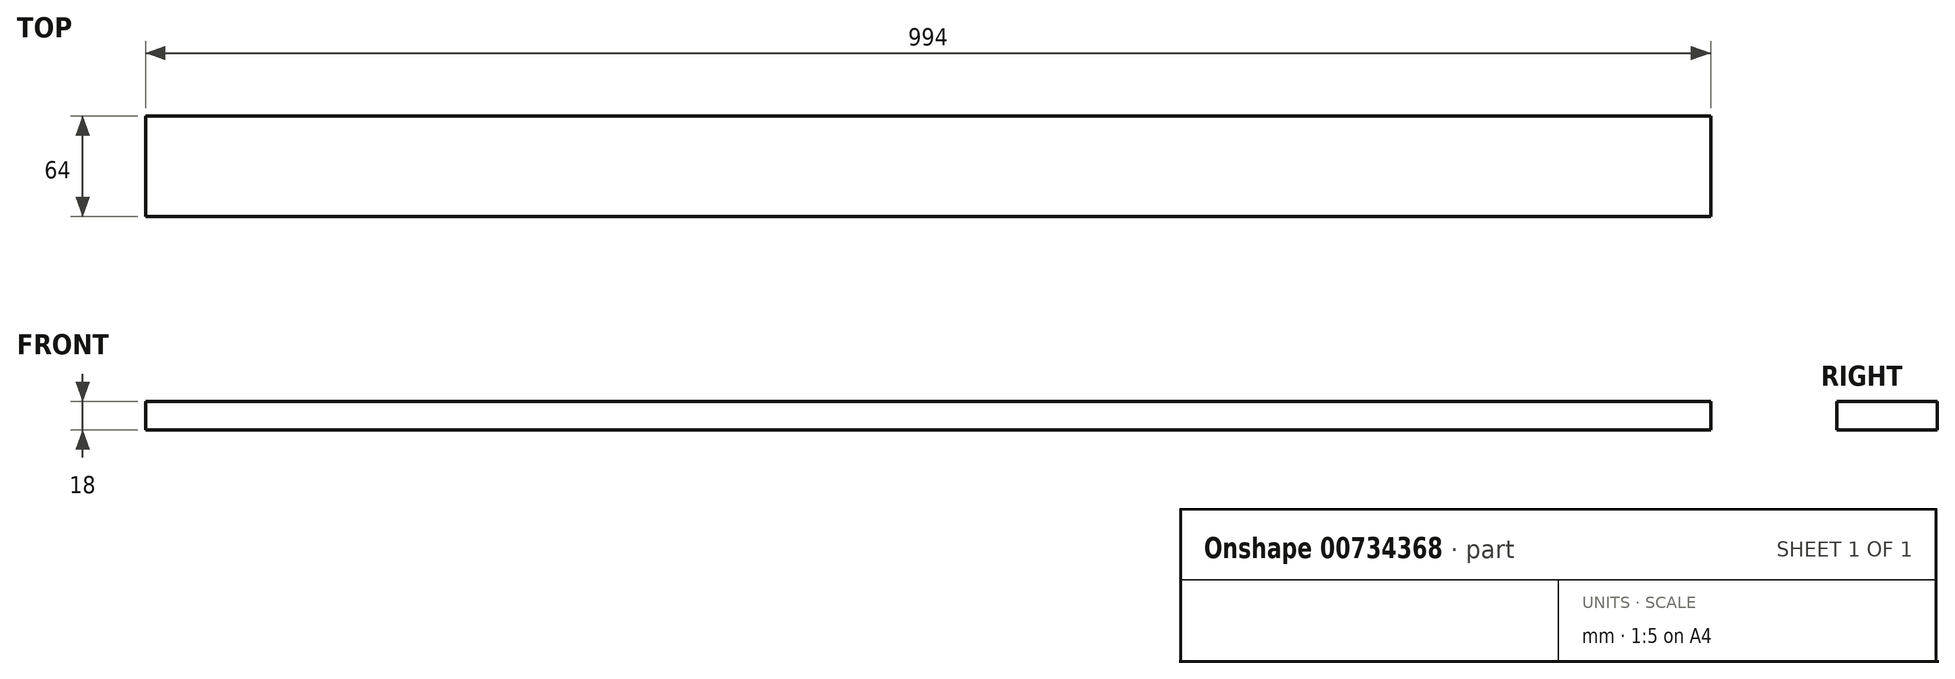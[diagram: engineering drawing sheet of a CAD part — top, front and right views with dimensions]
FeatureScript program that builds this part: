
annotation { "Feature Type Name" : "Feature", "Feature Type Description" : "" }
export const myFeature = defineFeature(function(context is Context, id is Id, definition is map)
    precondition{}
    {
        {
            var Q0;
            Q0=qCreatedBy(makeId("Top.planeOp"),FACE);
            var sketch = newSketch(context, id + "F0", { "sketchPlane" : qUnion([Q0])});
            skLineSegment(sketch, "E0.bottom", {"start": v(-497, -32) * mm, "end": v(497, -32) * mm});
            skLineSegment(sketch, "E0.top", {"start": v(-497, 32) * mm, "end": v(497, 32) * mm});
            skLineSegment(sketch, "E0.left", {"start": v(-497, -32) * mm, "end": v(-497, 32) * mm});
            skLineSegment(sketch, "E0.right", {"start": v(497, -32) * mm, "end": v(497, 32) * mm});
            skPoint(sketch, "E0.middle", {"position": v(0, 0) * mm});
            skSolve(sketch);
        }
        {
            var Q0;
            Q0 = qSketchRegion(id + "F0", true);
            extrude(context, id + "F1", {"entities" : qUnion([Q0]), "depth" : 18 * mm, "offsetDistance" : 25 * mm});
        }
    });
